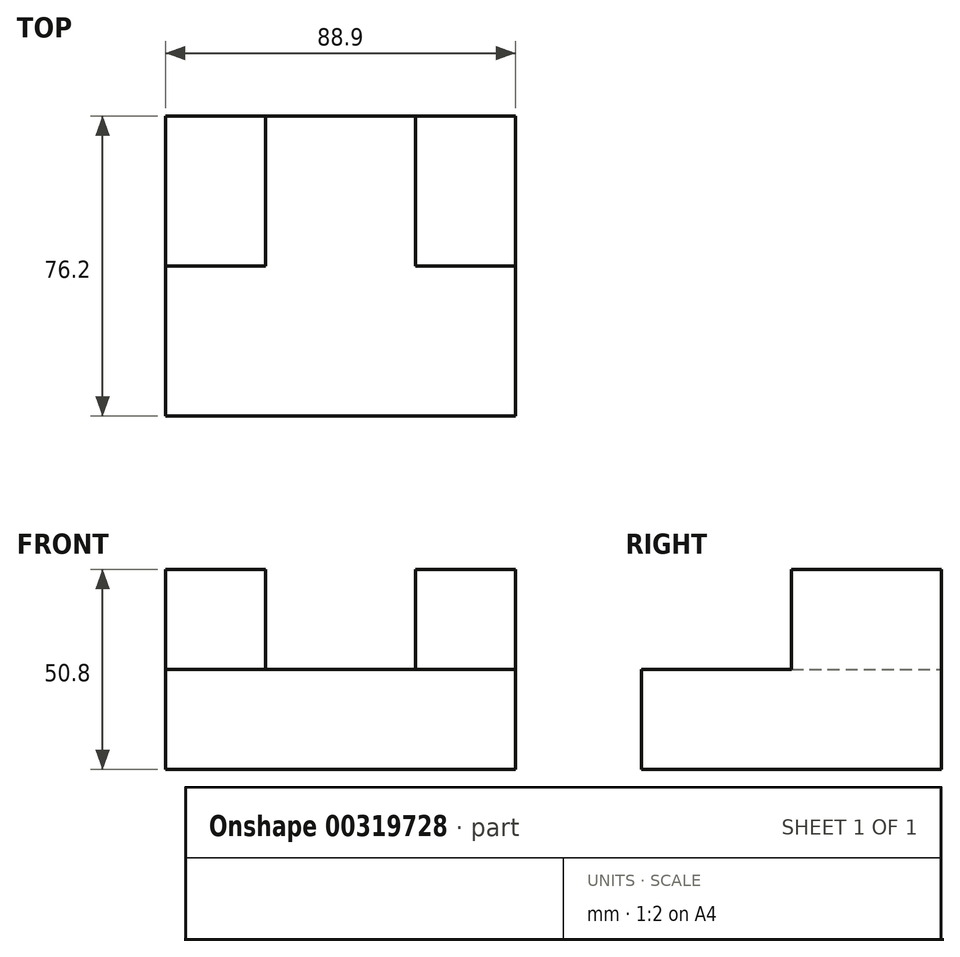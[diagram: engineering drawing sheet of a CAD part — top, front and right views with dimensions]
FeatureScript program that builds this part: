
annotation { "Feature Type Name" : "Feature", "Feature Type Description" : "" }
export const myFeature = defineFeature(function(context is Context, id is Id, definition is map)
    precondition{}
    {
        {
            var Q0;
            Q0=qCreatedBy(makeId("Top.planeOp"),FACE);
            var sketch = newSketch(context, id + "F0", { "sketchPlane" : qUnion([Q0])});
            skLineSegment(sketch, "E0", {"start": v(-40.91, 31.38) * mm, "end": v(-40.91, -44.82) * mm});
            skLineSegment(sketch, "E1", {"start": v(-40.91, -44.82) * mm, "end": v(47.99, -44.82) * mm});
            skLineSegment(sketch, "E2", {"start": v(47.99, -44.82) * mm, "end": v(47.99, 31.38) * mm});
            skLineSegment(sketch, "E3", {"start": v(47.99, 31.38) * mm, "end": v(-40.91, 31.38) * mm});
            skLineSegment(sketch, "E4", {"start": v(-40.91, -6.72) * mm, "end": v(-15.51, -6.72) * mm});
            skLineSegment(sketch, "E5", {"start": v(-15.51, -6.72) * mm, "end": v(-15.51, 31.38) * mm});
            skLineSegment(sketch, "E6", {"start": v(-15.51, 31.38) * mm, "end": v(-40.91, 31.38) * mm});
            skLineSegment(sketch, "E7", {"start": v(47.99, -6.72) * mm, "end": v(22.59, -6.72) * mm});
            skLineSegment(sketch, "E8", {"start": v(22.59, -6.72) * mm, "end": v(22.59, 31.38) * mm});
            skLineSegment(sketch, "E9", {"start": v(22.59, 31.38) * mm, "end": v(47.99, 31.38) * mm});
            skSolve(sketch);
        }
        {
            var Q0;
            {var subQ1=sQuery(id+"F0.wireOp",EDGE,"E1");Q0=makeQuery(id+"F0.imprint","IMPRINT",FACE,{"disambiguationData":[TD([[makeQuery(id+"F0.imprint","IMPRINT",EDGE,{"derivedFrom":subQ1}),1.0]])]});}
            var Q1;
            Q1=makeQuery(id+"F0.imprint","IMPRINT",FACE,{"disambiguationData":[TD([[makeQuery(id+"F0.imprint","IMPRINT",EDGE,{"derivedFrom":sQuery(id+"F0.wireOp",EDGE,"E5")}),1.0]])]});
            var Q2;
            Q2=makeQuery(id+"F0.imprint","IMPRINT",FACE,{"disambiguationData":[TD([[makeQuery(id+"F0.imprint","IMPRINT",EDGE,{"derivedFrom":sQuery(id+"F0.wireOp",EDGE,"E8")}),-1.0]])]});
            extrude(context, id + "F1", {"entities" : qUnion([Q0, Q1, Q2]), "oppositeDirection" : true, "depth" : 25.4 * mm});
        }
        {
            var Q0;
            Q0=makeQuery(id+"F0.imprint","IMPRINT",FACE,{"disambiguationData":[TD([[makeQuery(id+"F0.imprint","IMPRINT",EDGE,{"derivedFrom":sQuery(id+"F0.wireOp",EDGE,"E5")}),1.0]])]});
            var Q1;
            Q1=makeQuery(id+"F0.imprint","IMPRINT",FACE,{"disambiguationData":[TD([[makeQuery(id+"F0.imprint","IMPRINT",EDGE,{"derivedFrom":sQuery(id+"F0.wireOp",EDGE,"E8")}),-1.0]])]});
            extrude(context, id + "F2", {"entities" : qUnion([Q0, Q1]), "operationType" : NewBodyOperationType.ADD, "depth" : 25.4 * mm});
        }
    });
